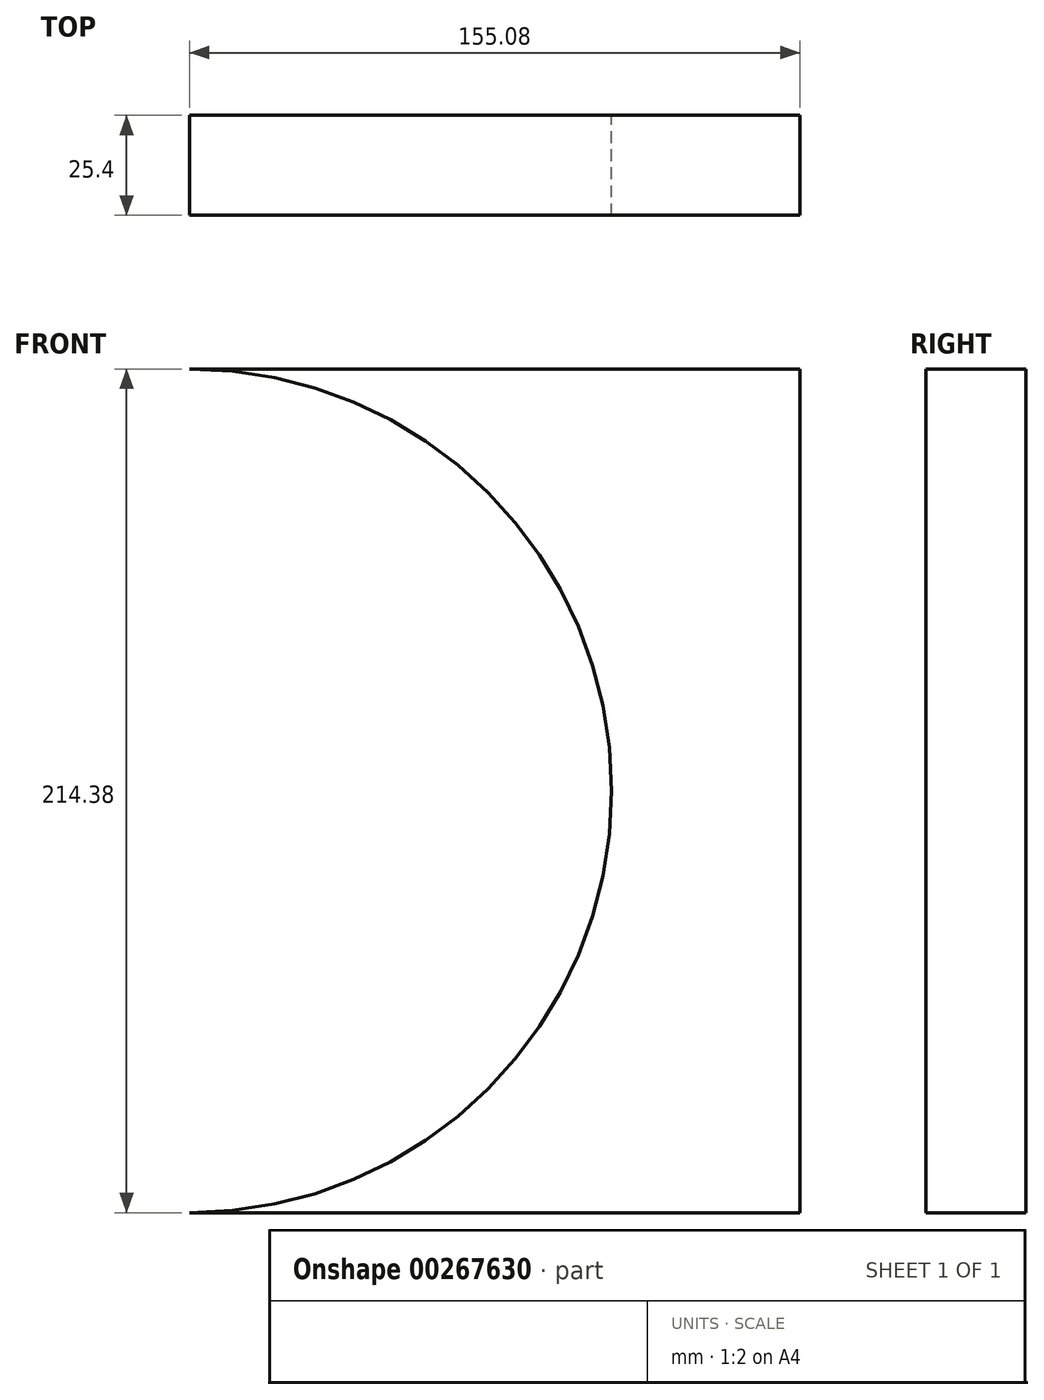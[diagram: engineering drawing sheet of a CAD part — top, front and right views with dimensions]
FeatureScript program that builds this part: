
annotation { "Feature Type Name" : "Feature", "Feature Type Description" : "" }
export const myFeature = defineFeature(function(context is Context, id is Id, definition is map)
    precondition{}
    {
        {
            var Q0;
            Q0=qCreatedBy(makeId("Front.planeOp"),FACE);
            var sketch = newSketch(context, id + "F0", { "sketchPlane" : qUnion([Q0])});
            skArc(sketch, "E0", {"start": v(0, -107.19) * mm, "mid": v(107.19, 0) * mm, "end": v(0, 107.19) * mm});
            skLineSegment(sketch, "E1.bottom", {"start": v(0, 107.19) * mm, "end": v(155.08, 107.19) * mm});
            skLineSegment(sketch, "E1.top", {"start": v(0, -107.19) * mm, "end": v(155.08, -107.19) * mm});
            skLineSegment(sketch, "E1.left", {"start": v(0, 107.19) * mm, "end": v(0, -107.19) * mm});
            skLineSegment(sketch, "E1.right", {"start": v(155.08, 107.19) * mm, "end": v(155.08, -107.19) * mm});
            skSolve(sketch);
        }
        {
            var Q0;
            Q0=makeQuery(id+"F0.imprint","IMPRINT",FACE,{"disambiguationData":[TD([[makeQuery(id+"F0.imprint","IMPRINT",EDGE,{"derivedFrom":sQuery(id+"F0.wireOp",EDGE,"E0")}),-1.0]])]});
            extrude(context, id + "F1", {"entities" : qUnion([Q0]), "depth" : 25.4 * mm});
        }
    });
